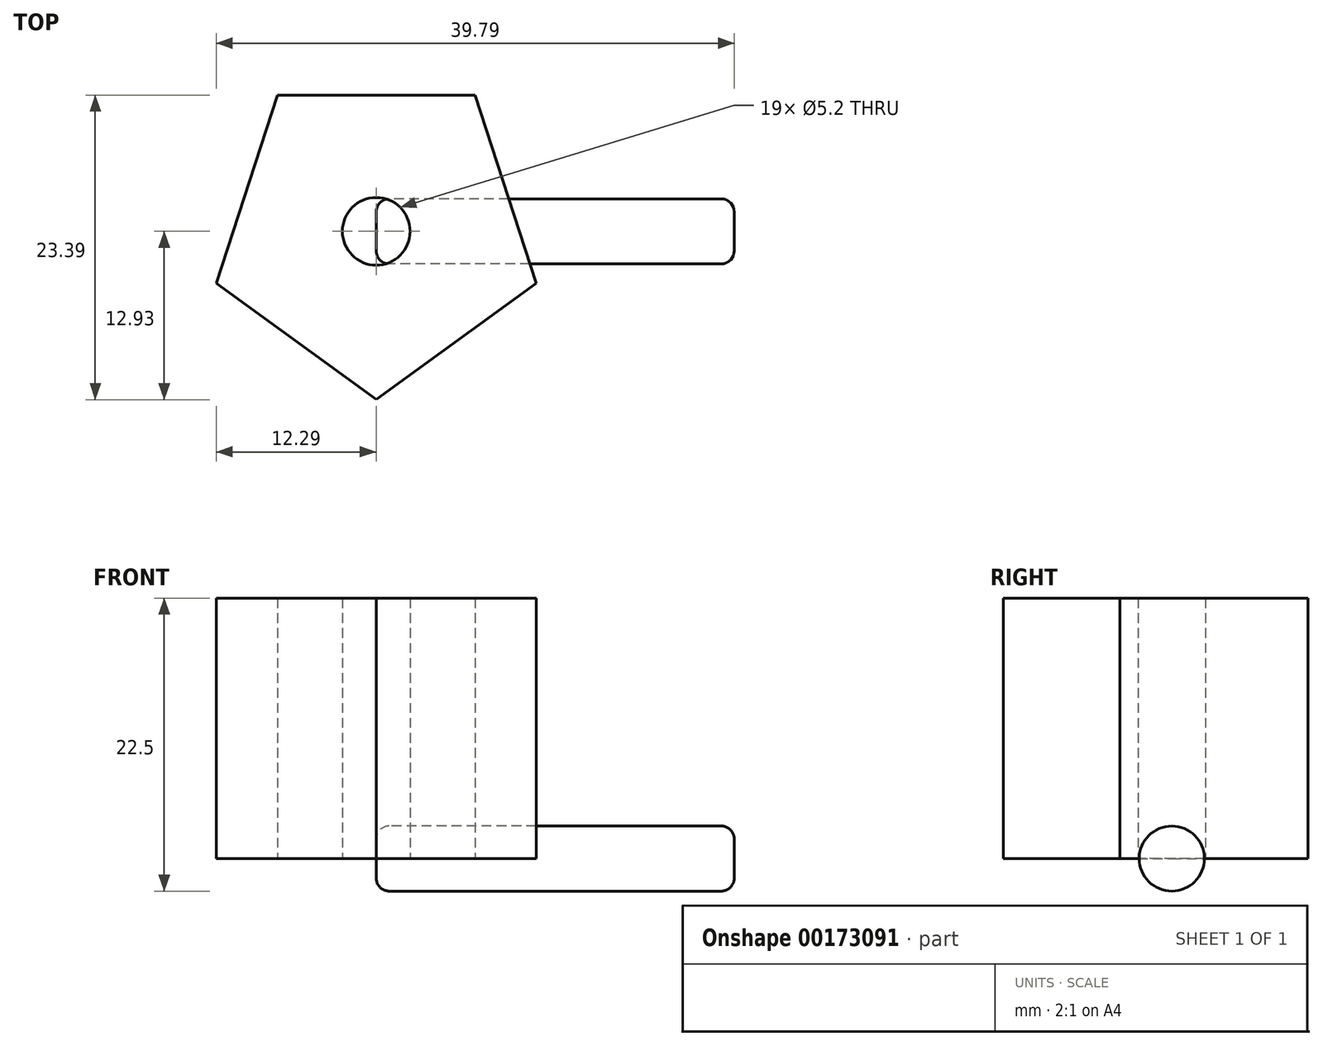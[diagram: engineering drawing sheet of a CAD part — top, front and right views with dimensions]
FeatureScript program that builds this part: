
annotation { "Feature Type Name" : "Feature", "Feature Type Description" : "" }
export const myFeature = defineFeature(function(context is Context, id is Id, definition is map)
    precondition{}
    {
        {
            var Q0;
            Q0=qCreatedBy(makeId("Right.planeOp"),FACE);
            var sketch = newSketch(context, id + "F0", { "sketchPlane" : qUnion([Q0])});
            skCircle(sketch, "E0", {"center": v(0, 0) * mm, "radius": 2.5 * mm});
            skSolve(sketch);
        }
        {
            var Q0;
            Q0=makeQuery(id+"F0.imprint","IMPRINT",FACE,{"disambiguationData":[TD([[makeQuery(id+"F0.imprint","IMPRINT",EDGE,{"derivedFrom":sQuery(id+"F0.wireOp",EDGE,"E0")}),1.0]])]});
            extrude(context, id + "F1", {"entities" : qUnion([Q0]), "depth" : 27.5 * mm});
        }
        {
            var Q0;
            Q0=makeQuery(id+"F1.opExtrude","CAP_EDGE",EDGE,{"disambiguationData":[OSD([sQuery(id+"F0.wireOp",EDGE,"E0")])],"isStart":false});
            var Q1;
            Q1=makeQuery(id+"F1.opExtrude","CAP_EDGE",EDGE,{"disambiguationData":[OSD([sQuery(id+"F0.wireOp",EDGE,"E0")])],"isStart":true});
            fillet(context, id + "F2", {"entities" : qUnion([Q0, Q1]), "radius" : 1 * mm, "tangentPropagation" : true, "allowEdgeOverflow" : false});
        }
        {
            var Q0;
            Q0=qCreatedBy(makeId("Top.planeOp"),FACE);
            var sketch = newSketch(context, id + "F3", { "sketchPlane" : qUnion([Q0])});
            skCircle(sketch, "E1", {"center": v(0, 0) * mm, "radius": 12.93 * mm, "construction": true});
            skCircle(sketch, "E2", {"center": v(0, 0) * mm, "radius": 2.6 * mm});
            skLineSegment(sketch, "E3.0", {"start": v(0, -12.93) * mm, "end": v(-12.3, -4) * mm});
            skLineSegment(sketch, "E3.1", {"start": v(-12.3, -4) * mm, "end": v(-7.6, 10.46) * mm});
            skLineSegment(sketch, "E3.2", {"start": v(-7.6, 10.46) * mm, "end": v(7.6, 10.46) * mm});
            skLineSegment(sketch, "E3.3", {"start": v(7.6, 10.46) * mm, "end": v(12.3, -4) * mm});
            skLineSegment(sketch, "E3.4", {"start": v(12.3, -4) * mm, "end": v(0, -12.93) * mm});
            skSolve(sketch);
        }
        {
            var Q0;
            Q0=makeQuery(id+"F3.imprint","IMPRINT",FACE,{"disambiguationData":[TD([[makeQuery(id+"F3.imprint","IMPRINT",EDGE,{"derivedFrom":sQuery(id+"F3.wireOp",EDGE,"E2")}),-1.0]])]});
            extrude(context, id + "F4", {"entities" : qUnion([Q0]), "depth" : 20 * mm});
        }
    });
